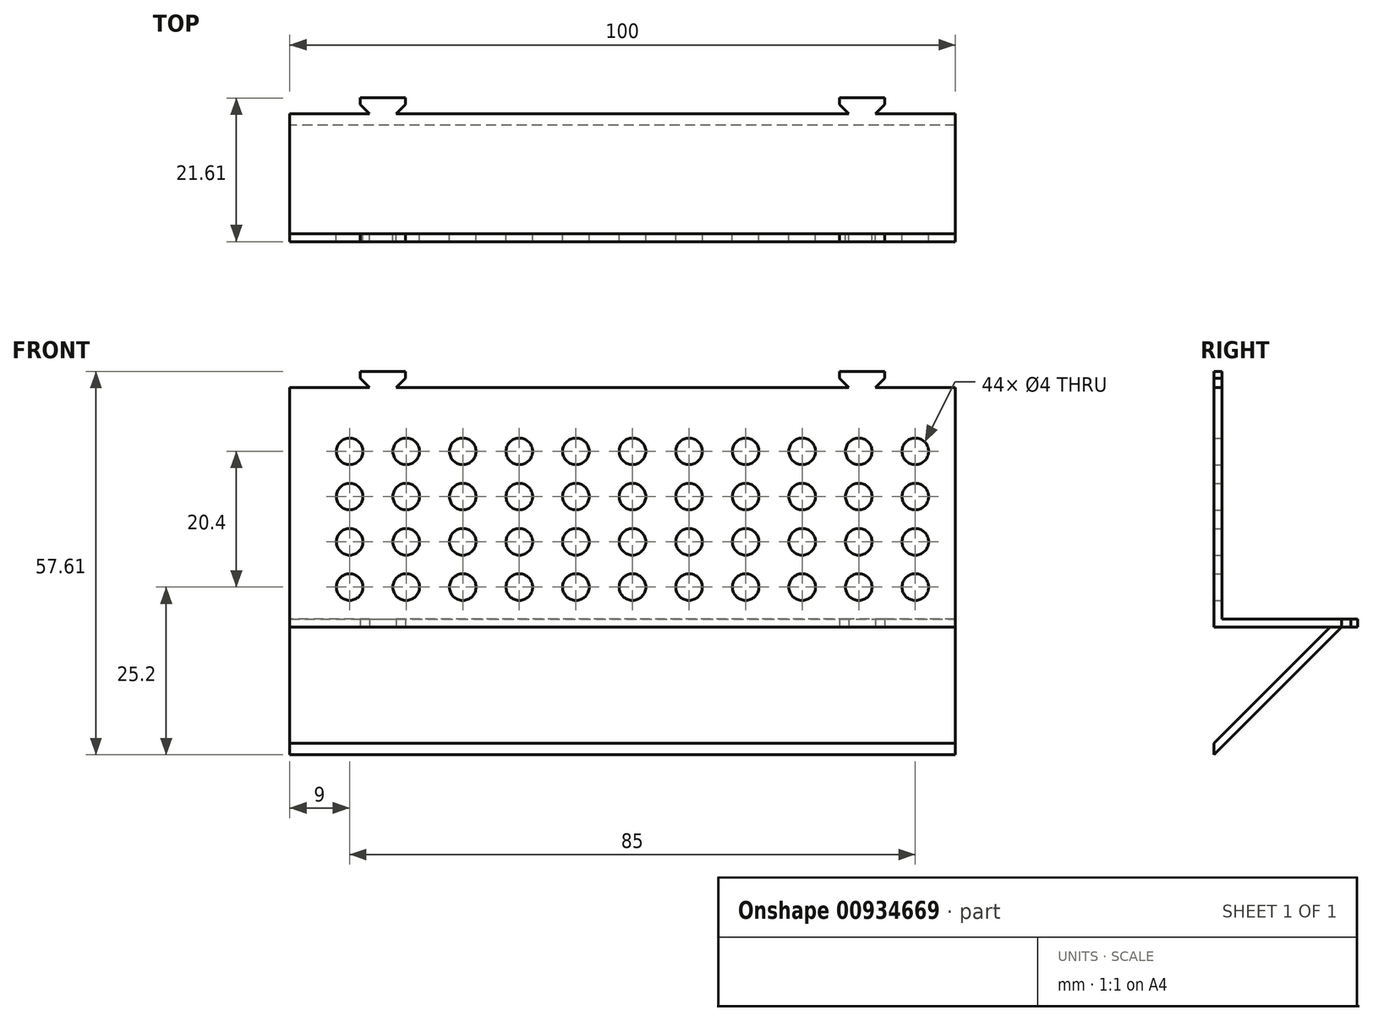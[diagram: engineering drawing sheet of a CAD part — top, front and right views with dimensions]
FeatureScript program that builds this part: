
annotation { "Feature Type Name" : "Feature", "Feature Type Description" : "" }
export const myFeature = defineFeature(function(context is Context, id is Id, definition is map)
    precondition{}
    {
        {
            var Q0;
            Q0=qCreatedBy(makeId("Front.planeOp"),FACE);
            var sketch = newSketch(context, id + "F0", { "sketchPlane" : qUnion([Q0])});
            skLineSegment(sketch, "E0.bottom", {"start": v(0, 0) * mm, "end": v(100, 0) * mm});
            skLineSegment(sketch, "E0.left", {"start": v(0, 0) * mm, "end": v(0, 36) * mm});
            skLineSegment(sketch, "E0.right", {"start": v(100, 0) * mm, "end": v(100, 36) * mm});
            skLineSegment(sketch, "E1", {"start": v(50, 36) * mm, "end": v(50, 0) * mm, "construction": true});
            skLineSegment(sketch, "E2", {"start": v(88, 36) * mm, "end": v(89.41, 37.41) * mm});
            skLineSegment(sketch, "E3", {"start": v(89.41, 37.41) * mm, "end": v(89.41, 38.41) * mm});
            skLineSegment(sketch, "E4", {"start": v(89.41, 38.41) * mm, "end": v(82.59, 38.41) * mm});
            skLineSegment(sketch, "E5", {"start": v(82.59, 38.41) * mm, "end": v(82.59, 37.41) * mm});
            skLineSegment(sketch, "E6", {"start": v(82.59, 37.41) * mm, "end": v(84, 36) * mm});
            skLineSegment(sketch, "E7.MirrorCS", {"start": v(17.41, 37.41) * mm, "end": v(16, 36) * mm});
            skLineSegment(sketch, "E8.MirrorCS", {"start": v(17.41, 38.41) * mm, "end": v(17.41, 37.41) * mm});
            skLineSegment(sketch, "E9.MirrorCS", {"start": v(10.59, 38.41) * mm, "end": v(17.41, 38.41) * mm});
            skLineSegment(sketch, "E10.MirrorCS", {"start": v(10.59, 37.41) * mm, "end": v(10.59, 38.41) * mm});
            skLineSegment(sketch, "E11.MirrorCS", {"start": v(12, 36) * mm, "end": v(10.59, 37.41) * mm});
            skLineSegment(sketch, "E12", {"start": v(100, 36) * mm, "end": v(88, 36) * mm});
            skLineSegment(sketch, "E13", {"start": v(84, 36) * mm, "end": v(16, 36) * mm});
            skLineSegment(sketch, "E14", {"start": v(12, 36) * mm, "end": v(0, 36) * mm});
            skLineSegment(sketch, "E15", {"start": v(100, 36) * mm, "end": v(0, 36) * mm, "construction": true});
            skCircle(sketch, "E16", {"center": v(94, 6) * mm, "radius": 2 * mm});
            skCircle(sketch, "E17.0.1.0", {"center": v(94, 12.8) * mm, "radius": 2 * mm});
            skCircle(sketch, "E17.0.2.0", {"center": v(94, 19.6) * mm, "radius": 2 * mm});
            skCircle(sketch, "E17.1.0.0", {"center": v(85.5, 6) * mm, "radius": 2 * mm});
            skCircle(sketch, "E17.1.1.0", {"center": v(85.5, 12.8) * mm, "radius": 2 * mm});
            skCircle(sketch, "E17.1.2.0", {"center": v(85.5, 19.6) * mm, "radius": 2 * mm});
            skCircle(sketch, "E17.2.0.0", {"center": v(77, 6) * mm, "radius": 2 * mm});
            skCircle(sketch, "E17.2.1.0", {"center": v(77, 12.8) * mm, "radius": 2 * mm});
            skCircle(sketch, "E17.2.2.0", {"center": v(77, 19.6) * mm, "radius": 2 * mm});
            skCircle(sketch, "E17.3.0.0", {"center": v(68.5, 6) * mm, "radius": 2 * mm});
            skCircle(sketch, "E17.3.1.0", {"center": v(68.5, 12.8) * mm, "radius": 2 * mm});
            skCircle(sketch, "E17.3.2.0", {"center": v(68.5, 19.6) * mm, "radius": 2 * mm});
            skCircle(sketch, "E17.4.0.0", {"center": v(60, 6) * mm, "radius": 2 * mm});
            skCircle(sketch, "E17.4.1.0", {"center": v(60, 12.8) * mm, "radius": 2 * mm});
            skCircle(sketch, "E17.4.2.0", {"center": v(60, 19.6) * mm, "radius": 2 * mm});
            skCircle(sketch, "E17.5.0.0", {"center": v(51.5, 6) * mm, "radius": 2 * mm});
            skCircle(sketch, "E17.5.1.0", {"center": v(51.5, 12.8) * mm, "radius": 2 * mm});
            skCircle(sketch, "E17.5.2.0", {"center": v(51.5, 19.6) * mm, "radius": 2 * mm});
            skCircle(sketch, "E17.6.0.0", {"center": v(43, 6) * mm, "radius": 2 * mm});
            skCircle(sketch, "E17.6.1.0", {"center": v(43, 12.8) * mm, "radius": 2 * mm});
            skCircle(sketch, "E17.6.2.0", {"center": v(43, 19.6) * mm, "radius": 2 * mm});
            skCircle(sketch, "E17.7.0.0", {"center": v(34.5, 6) * mm, "radius": 2 * mm});
            skCircle(sketch, "E17.7.1.0", {"center": v(34.5, 12.8) * mm, "radius": 2 * mm});
            skCircle(sketch, "E17.7.2.0", {"center": v(34.5, 19.6) * mm, "radius": 2 * mm});
            skCircle(sketch, "E17.8.0.0", {"center": v(26, 6) * mm, "radius": 2 * mm});
            skCircle(sketch, "E17.8.1.0", {"center": v(26, 12.8) * mm, "radius": 2 * mm});
            skCircle(sketch, "E17.8.2.0", {"center": v(26, 19.6) * mm, "radius": 2 * mm});
            skLineSegment(sketch, "E17.direction1", {"start": v(74, 6) * mm, "end": v(65.5, 6) * mm, "construction": true});
            skLineSegment(sketch, "E17.direction2", {"start": v(74, 6) * mm, "end": v(74, 12.8) * mm, "construction": true});
            skCircle(sketch, "E18.0.0.3", {"center": v(94, 26.4) * mm, "radius": 2 * mm});
            skCircle(sketch, "E18.0.1.3", {"center": v(85.5, 26.4) * mm, "radius": 2 * mm});
            skCircle(sketch, "E18.0.2.3", {"center": v(77, 26.4) * mm, "radius": 2 * mm});
            skCircle(sketch, "E18.0.3.3", {"center": v(68.5, 26.4) * mm, "radius": 2 * mm});
            skCircle(sketch, "E18.0.4.3", {"center": v(60, 26.4) * mm, "radius": 2 * mm});
            skCircle(sketch, "E18.0.5.3", {"center": v(51.5, 26.4) * mm, "radius": 2 * mm});
            skCircle(sketch, "E18.0.6.3", {"center": v(43, 26.4) * mm, "radius": 2 * mm});
            skCircle(sketch, "E18.0.7.3", {"center": v(34.5, 26.4) * mm, "radius": 2 * mm});
            skCircle(sketch, "E18.0.8.3", {"center": v(26, 26.4) * mm, "radius": 2 * mm});
            skCircle(sketch, "E19.0.9.0", {"center": v(17.5, 6) * mm, "radius": 2 * mm});
            skCircle(sketch, "E19.0.9.1", {"center": v(17.5, 12.8) * mm, "radius": 2 * mm});
            skCircle(sketch, "E19.0.9.2", {"center": v(17.5, 19.6) * mm, "radius": 2 * mm});
            skCircle(sketch, "E19.0.9.3", {"center": v(17.5, 26.4) * mm, "radius": 2 * mm});
            skCircle(sketch, "E19.0.10.0", {"center": v(9, 6) * mm, "radius": 2 * mm});
            skCircle(sketch, "E19.0.10.1", {"center": v(9, 12.8) * mm, "radius": 2 * mm});
            skCircle(sketch, "E19.0.10.2", {"center": v(9, 19.6) * mm, "radius": 2 * mm});
            skCircle(sketch, "E19.0.10.3", {"center": v(9, 26.4) * mm, "radius": 2 * mm});
            skSolve(sketch);
        }
        {
            var Q0;
            Q0=makeQuery(id+"F0.imprint","IMPRINT",FACE,{"disambiguationData":[TD([[makeQuery(id+"F0.imprint","IMPRINT",EDGE,{"derivedFrom":sQuery(id+"F0.wireOp",EDGE,"E0.bottom")}),1.0]])]});
            extrude(context, id + "F1", {"entities" : qUnion([Q0]), "depth" : 1.2 * mm, "offsetDistance" : 25 * mm});
        }
        {
            var Q0;
            Q0=qCreatedBy(makeId("Top.planeOp"),FACE);
            var sketch = newSketch(context, id + "F2", { "sketchPlane" : qUnion([Q0])});
            skLineSegment(sketch, "E20.bottom", {"start": v(0, 0) * mm, "end": v(100, 0) * mm});
            skLineSegment(sketch, "E20.left", {"start": v(0, 0) * mm, "end": v(0, 18) * mm});
            skLineSegment(sketch, "E20.right", {"start": v(100, 0) * mm, "end": v(100, 18) * mm});
            skLineSegment(sketch, "E21", {"start": v(50, 18) * mm, "end": v(50, 0) * mm, "construction": true});
            skLineSegment(sketch, "E22", {"start": v(88, 18) * mm, "end": v(89.41, 19.41) * mm});
            skLineSegment(sketch, "E23", {"start": v(89.41, 19.41) * mm, "end": v(89.41, 20.41) * mm});
            skLineSegment(sketch, "E24", {"start": v(89.41, 20.41) * mm, "end": v(82.59, 20.41) * mm});
            skLineSegment(sketch, "E25", {"start": v(82.59, 20.41) * mm, "end": v(82.59, 19.41) * mm});
            skLineSegment(sketch, "E26", {"start": v(82.59, 19.41) * mm, "end": v(84, 18) * mm});
            skLineSegment(sketch, "E27.MirrorCS", {"start": v(17.41, 19.41) * mm, "end": v(16, 18) * mm});
            skLineSegment(sketch, "E28.MirrorCS", {"start": v(17.41, 20.41) * mm, "end": v(17.41, 19.41) * mm});
            skLineSegment(sketch, "E29.MirrorCS", {"start": v(10.59, 20.41) * mm, "end": v(17.41, 20.41) * mm});
            skLineSegment(sketch, "E30.MirrorCS", {"start": v(10.59, 19.41) * mm, "end": v(10.59, 20.41) * mm});
            skLineSegment(sketch, "E31.MirrorCS", {"start": v(12, 18) * mm, "end": v(10.59, 19.41) * mm});
            skLineSegment(sketch, "E32", {"start": v(100, 18) * mm, "end": v(88, 18) * mm});
            skLineSegment(sketch, "E33", {"start": v(84, 18) * mm, "end": v(16, 18) * mm});
            skLineSegment(sketch, "E34", {"start": v(12, 18) * mm, "end": v(0, 18) * mm});
            skLineSegment(sketch, "E35", {"start": v(100, 18) * mm, "end": v(0, 18) * mm, "construction": true});
            skSolve(sketch);
        }
        {
            var Q0;
            Q0=makeQuery(id+"F2.imprint","IMPRINT",FACE,{"disambiguationData":[TD([[makeQuery(id+"F2.imprint","IMPRINT",EDGE,{"derivedFrom":sQuery(id+"F2.wireOp",EDGE,"E20.bottom")}),1.0]])]});
            extrude(context, id + "F3", {"entities" : qUnion([Q0]), "operationType" : NewBodyOperationType.ADD, "depth" : 1.2 * mm, "offsetDistance" : 25 * mm});
        }
        {
            var Q0;
            Q0=makeQuery(id+"F3.boolean.opBoolean","MERGE",FACE,{"derivedFrom":[makeQuery(id+"F1.opExtrude","SWEPT_FACE",FACE,{"disambiguationData":[OSD([sQuery(id+"F0.wireOp",EDGE,"E0.left")])]}),makeQuery(id+"F3.opExtrude","SWEPT_FACE",FACE,{"disambiguationData":[OSD([sQuery(id+"F2.wireOp",EDGE,"E20.left")])]})]});
            var sketch = newSketch(context, id + "F4", { "sketchPlane" : qUnion([Q0])});
            skLineSegment(sketch, "E36", {"start": v(1.2, -17.5) * mm, "end": v(1.2, -19.2) * mm});
            skLineSegment(sketch, "E37", {"start": v(1.2, -19.2) * mm, "end": v(-18, 0) * mm});
            skLineSegment(sketch, "E38", {"start": v(-18, 0) * mm, "end": v(-16.3, 0) * mm});
            skLineSegment(sketch, "E39", {"start": v(-16.3, 0) * mm, "end": v(1.2, -17.5) * mm});
            skSolve(sketch);
        }
        {
            var Q0;
            Q0=makeQuery(id+"F4.imprint","IMPRINT",FACE,{"disambiguationData":[TD([[makeQuery(id+"F4.imprint","IMPRINT",EDGE,{"derivedFrom":sQuery(id+"F4.wireOp",EDGE,"E36")}),-1.0]])]});
            extrude(context, id + "F5", {"entities" : qUnion([Q0]), "oppositeDirection" : true, "depth" : 100 * mm, "offsetDistance" : 25 * mm});
        }
    });
